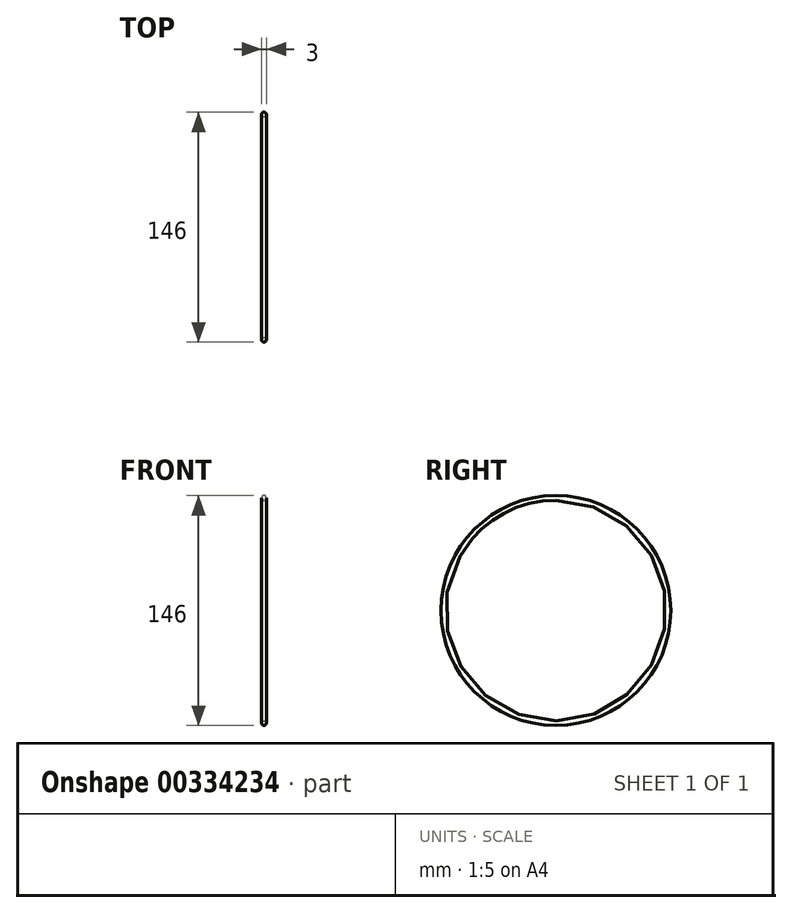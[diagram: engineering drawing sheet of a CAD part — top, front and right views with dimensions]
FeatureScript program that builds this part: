
annotation { "Feature Type Name" : "Feature", "Feature Type Description" : "" }
export const myFeature = defineFeature(function(context is Context, id is Id, definition is map)
    precondition{}
    {
        {
            var Q0;
            Q0=qCreatedBy(makeId("Right.planeOp"),FACE);
            var sketch = newSketch(context, id + "F0", { "sketchPlane" : qUnion([Q0])});
            skCircle(sketch, "E0", {"center": v(0, 0) * mm, "radius": 71.5 * mm});
            skSolve(sketch);
        }
        {
            var Q0;
            Q0=qCreatedBy(makeId("Front.planeOp"),FACE);
            var sketch = newSketch(context, id + "F1", { "sketchPlane" : qUnion([Q0])});
            skCircle(sketch, "E1", {"center": v(0, 71.5) * mm, "radius": 1.5 * mm});
            skSolve(sketch);
        }
        {
            var Q0;
            Q0=makeQuery(id+"F1.imprint","IMPRINT",FACE,{"disambiguationData":[TD([[makeQuery(id+"F1.imprint","IMPRINT",EDGE,{"derivedFrom":sQuery(id+"F1.wireOp",EDGE,"E1")}),1.0]])]});
            var Q1;
            Q1=sQuery(id+"F0.wireOp",EDGE,"E0");
            revolve(context, id + "F2", {"entities" : qUnion([Q0]), "axis" : qUnion([Q1]), "revolveType" : RevolveType.FULL});
        }
    });
